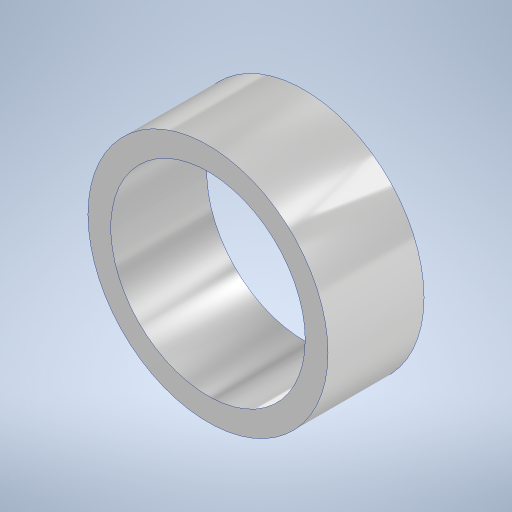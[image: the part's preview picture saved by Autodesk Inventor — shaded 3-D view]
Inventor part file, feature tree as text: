
AUTODESK INVENTOR PART (.ipt)
format: ipt  version: 2024 (Build 280153000, 153)  size: 250,368 bytes
history: native  units: mm
features: extrude x1, sketch x1
ambient origin geometry x8: Origin, YZ Plane, XZ Plane, XY Plane, X Axis, Y Axis, Z Axis, Center Point
bodies: Body1 (feature_tree)
feature tree (2):
  extrude  "Extrusion2"  Depth=4.0mm
  sketch  "Sketch2"  dims[d4=10.0mm d5=8.1mm d6=4.0mm d7=0.0mm]
